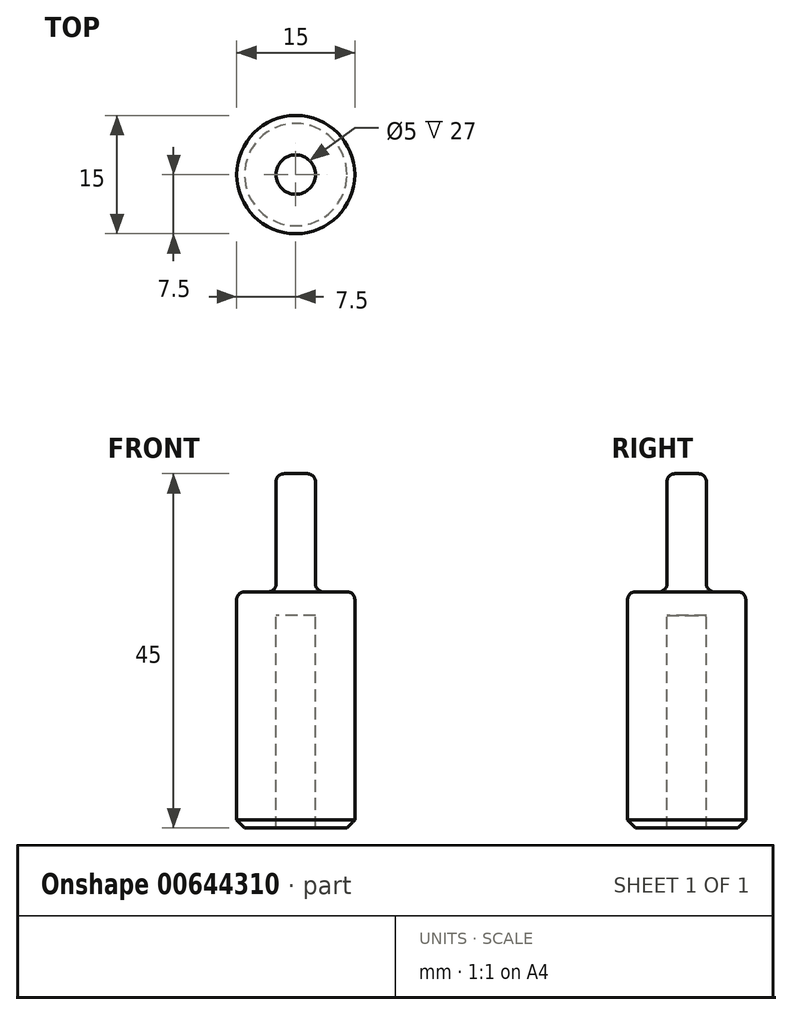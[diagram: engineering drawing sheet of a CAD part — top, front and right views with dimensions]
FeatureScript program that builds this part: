
annotation { "Feature Type Name" : "Feature", "Feature Type Description" : "" }
export const myFeature = defineFeature(function(context is Context, id is Id, definition is map)
    precondition{}
    {
        {
            var Q0;
            Q0=qCreatedBy(makeId("Right.planeOp"),FACE);
            var sketch = newSketch(context, id + "F0", { "sketchPlane" : qUnion([Q0])});
            skLineSegment(sketch, "E0", {"start": v(2.5, 0) * mm, "end": v(7.5, 0) * mm});
            skLineSegment(sketch, "E1", {"start": v(7.5, 0) * mm, "end": v(7.5, 30) * mm});
            skLineSegment(sketch, "E2", {"start": v(7.5, 30) * mm, "end": v(2.5, 30) * mm});
            skLineSegment(sketch, "E3", {"start": v(2.5, 30) * mm, "end": v(2.5, 45) * mm});
            skLineSegment(sketch, "E4", {"start": v(2.5, 45) * mm, "end": v(0, 45) * mm});
            skLineSegment(sketch, "E5", {"start": v(0, 44.74) * mm, "end": v(0, -19.14) * mm, "construction": true});
            skLineSegment(sketch, "E6", {"start": v(2.5, 0) * mm, "end": v(2.5, 27) * mm});
            skLineSegment(sketch, "E7", {"start": v(2.5, 27) * mm, "end": v(0, 27) * mm});
            skLineSegment(sketch, "E8", {"start": v(0, 27) * mm, "end": v(0, 45) * mm});
            skPoint(sketch, "E9.orphan", {"position": v(0, 45) * mm});
            skSolve(sketch);
        }
        {
            var Q0;
            Q0=qSketchRegion(id+"F0",true);
            var Q1;
            Q1=sQuery(id+"F0.wireOp",EDGE,"E5");
            revolve(context, id + "F1", {"entities" : qUnion([Q0]), "axis" : qUnion([Q1]), "revolveType" : RevolveType.FULL});
        }
        {
            var Q0;
            Q0=makeQuery(id+"F1.opRevolve","SWEPT_EDGE",EDGE,{"disambiguationData":[OSD([sQuery(id+"F0.wireOp",EDGE,"E3"),sQuery(id+"F0.wireOp",EDGE,"E4")])]});
            var Q1;
            Q1=makeQuery(id+"F1.opRevolve","SWEPT_EDGE",EDGE,{"disambiguationData":[OSD([sQuery(id+"F0.wireOp",EDGE,"E2"),sQuery(id+"F0.wireOp",EDGE,"E3")])]});
            var Q2;
            Q2=makeQuery(id+"F1.opRevolve","SWEPT_EDGE",EDGE,{"disambiguationData":[OSD([sQuery(id+"F0.wireOp",EDGE,"E1"),sQuery(id+"F0.wireOp",EDGE,"E2")])]});
            fillet(context, id + "F2", {"entities" : qUnion([Q0, Q1, Q2]), "radius" : 1 * mm, "tangentPropagation" : true, "allowEdgeOverflow" : false});
        }
        {
            var Q0;
            Q0=makeQuery(id+"F1.opRevolve","SWEPT_EDGE",EDGE,{"disambiguationData":[OSD([sQuery(id+"F0.wireOp",EDGE,"E0"),sQuery(id+"F0.wireOp",EDGE,"E1")])]});
            chamfer(context, id + "F3", {"entities" : qUnion([Q0]), "width" : 1 * mm, "tangentPropagation" : true});
        }
    });
